FREECAD ASSEMBLY — COMPONENT RECIPES ("YR_ASSEMBLED")

This assembly document has 4 components, labeled P0..P3 below (a component is one placed body or linked part). 4 of them carry a construction recipe — the FreeCAD feature program that regenerates the part from scratch, quoted from this document or its linked companion documents; the rest are supplied as boundary geometry only. No exploded tour is included for this assembly.
COMPONENT P0 — recipe-attached ("Body001", a linked part whose construction recipe lives in a companion FreeCAD document of the same project; that document's serialized recipe follows).
Construction recipe (the companion document, serialized — sketch geometry with constraints, then the solid features built on it; lengths are millimeters unless a unit is written):

FCSTD DOCUMENT  (FreeCAD 1.0R39319 (Git))
Label: knob
License: All rights reserved
LicenseURL: https://en.wikipedia.org/wiki/All_rights_reserved
objects: PartDesign::Chamfer×2, Sketcher::SketchObject×1, PartDesign::Pad×1, PartDesign::Body×1
note: 12 computed .brp shape members not serialized (recipe doc carries the construction recipe); baked Part::Feature solids carry a one-line shape summary decoded from their .brp

FEATURE [Sketcher::SketchObject] Sketch
  ArcFitTolerance = 1e-06
  AttachmentSupport = -> [XY_Plane]
  FullyConstrained = true
  MakeInternals = false
  MapMode = 5
  sketch-geometry (1):
    g0: Circle CenterX=0 CenterY=0 CenterZ=0 NormalX=0 NormalY=0 NormalZ=1 AngleXU=0 Radius=10.5
  constraints (2):
    c: Diameter(g0) = 21
    c: Coincident(g0,g-1)
FEATURE [PartDesign::Pad] Pad
  Direction = (0,0,1)
  Length = 17
  Length2 = 10
  Profile = -> Sketch
  ReferenceAxis = -> Sketch [N_Axis]
  Refine = true
  Suppressed = false
  Type = 0
FEATURE [PartDesign::Chamfer] Chamfer
  Angle = 45
  Base = -> Pad [Edge3]
  BaseFeature = -> Pad
  ChamferType = 0
  FlipDirection = false
  Refine = true
  Size = 1
  Size2 = 1
  SupportTransform = false
  Suppressed = false
  UseAllEdges = false
FEATURE [PartDesign::Chamfer] Chamfer001
  Angle = 45
  Base = -> Chamfer [Edge3]
  BaseFeature = -> Chamfer
  ChamferType = 0
  FlipDirection = false
  Refine = true
  Size = 1
  Size2 = 1
  SupportTransform = false
  Suppressed = false
  UseAllEdges = false
FEATURE [PartDesign::Body] Body
  AllowCompound = false
  Group = -> [Sketch,Pad,Chamfer,Chamfer001]
  Origin = -> Origin
  Tip = -> Chamfer001
COMPONENT P1 — recipe-attached ("ER-OLEDM032-1_new054", a linked part whose construction recipe lives in a companion FreeCAD document of the same project; that document's serialized recipe follows).
Construction recipe (the companion document, serialized — sketch geometry with constraints, then the solid features built on it; lengths are millimeters unless a unit is written):

FCSTD DOCUMENT  (FreeCAD 1.0R39319 (Git))
Label: SSD1322
License: All rights reserved
objects: Part::Feature×54, PartDesign::Body×1, App::Part×1
note: 55 computed .brp shape members not serialized (recipe doc carries the construction recipe); baked Part::Feature solids carry a one-line shape summary decoded from their .brp

FEATURE [PartDesign::Body] Body
  AllowCompound = false
  Origin = -> Origin
FEATURE [Part::Feature] Part__Feature  label="ER-OLEDM032-1_new"
  shape: bbox 100.5 x 33.5 x 1 mm, 110 faces (baked)
FEATURE [Part::Feature] Part__Feature001  label="ER-OLEDM032-1_new001"
  shape: bbox 3.007 x 3.014 x 2.1 mm, 6 faces (baked)
FEATURE [Part::Feature] Part__Feature002  label="ER-OLEDM032-1_new002"
  shape: bbox 3.007 x 3.014 x 2.1 mm, 6 faces (baked)
FEATURE [Part::Feature] Part__Feature003  label="ER-OLEDM032-1_new003"
  shape: bbox 3.007 x 3.014 x 2.1 mm, 6 faces (baked)
FEATURE [Part::Feature] Part__Feature004  label="ER-OLEDM032-1_new004"
  shape: bbox 3.007 x 3.014 x 2.1 mm, 6 faces (baked)
FEATURE [Part::Feature] Part__Feature005  label="ER-OLEDM032-1_new005"
  shape: bbox 3.007 x 3.014 x 2.1 mm, 6 faces (baked)
FEATURE [Part::Feature] Part__Feature006  label="ER-OLEDM032-1_new006"
  shape: bbox 5.7 x 3.24 x 2.3 mm, 6 faces (baked)
FEATURE [Part::Feature] Part__Feature007  label="ER-OLEDM032-1_new007"
  shape: bbox 1.746 x 1.036 x 0.1 mm, 14 faces (baked)
FEATURE [Part::Feature] Part__Feature008  label="ER-OLEDM032-1_new008"
  shape: bbox 1.751 x 1.201 x 0.1 mm, 17 faces (baked)
FEATURE [Part::Feature] Part__Feature009  label="ER-OLEDM032-1_new009"
  shape: bbox 0.1525 x 0.6143 x 0.1 mm, 6 faces (baked)
FEATURE [Part::Feature] Part__Feature010  label="ER-OLEDM032-1_new010"
  shape: bbox 1.792 x 1.506 x 0.1 mm, 12 faces (baked)
FEATURE [Part::Feature] Part__Feature011  label="ER-OLEDM032-1_new011"
  shape: bbox 1.748 x 0.9883 x 0.1 mm, 8 faces (baked)
FEATURE [Part::Feature] Part__Feature012  label="ER-OLEDM032-1_new012"
  shape: bbox 1.746 x 1.036 x 0.1 mm, 14 faces (baked)
FEATURE [Part::Feature] Part__Feature013  label="ER-OLEDM032-1_new013"
  shape: bbox 1.748 x 1.262 x 0.1 mm, 12 faces (baked)
FEATURE [Part::Feature] Part__Feature014  label="ER-OLEDM032-1_new014"
  shape: bbox 1.75 x 1.462 x 0.1 mm, 24 faces (baked)
FEATURE [Part::Feature] Part__Feature015  label="ER-OLEDM032-1_new015"
  shape: bbox 1.795 x 1.062 x 0.1 mm, 12 faces (baked)
FEATURE [Part::Feature] Part__Feature016  label="ER-OLEDM032-1_new016"
  shape: bbox 1.792 x 1.13 x 0.1 mm, 19 faces (baked)
FEATURE [Part::Feature] Part__Feature017  label="ER-OLEDM032-1_new017"
  shape: bbox 1.77 x 1.096 x 0.1 mm, 14 faces (baked)
FEATURE [Part::Feature] Part__Feature018  label="ER-OLEDM032-1_new018"
  shape: bbox 0.1525 x 0.6143 x 0.1 mm, 6 faces (baked)
FEATURE [Part::Feature] Part__Feature019  label="ER-OLEDM032-1_new019"
  shape: bbox 1.748 x 0.9421 x 0.1 mm, 13 faces (baked)
FEATURE [Part::Feature] Part__Feature020  label="ER-OLEDM032-1_new020"
  shape: bbox 57 x 18.36 x 3 mm, 48 faces (baked)
FEATURE [Part::Feature] Part__Feature021  label="ER-OLEDM032-1_new021"
  shape: bbox 85 x 26 x 1.8 mm, 7 faces (baked)
FEATURE [Part::Feature] Part__Feature022  label="ER-OLEDM032-1_new022"
  shape: bbox 89.5 x 30.8 x 3 mm, 60 faces (baked)
FEATURE [Part::Feature] Part__Feature023  label="ER-OLEDM032-1_new023"
  shape: bbox 9.982 x 0.1017 x 0.2 mm, 6 faces (baked)
FEATURE [Part::Feature] Part__Feature024  label="ER-OLEDM032-1_new024"
  shape: bbox 1.086 x 4.946 x 0.2 mm, 5 faces (baked)
FEATURE [Part::Feature] Part__Feature025  label="ER-OLEDM032-1_new025"
  shape: bbox 3.64 x 4.408 x 0.2 mm, 10 faces (baked)
FEATURE [Part::Feature] Part__Feature026  label="ER-OLEDM032-1_new026"
  shape: bbox 2.025 x 2.903 x 0.2 mm, 8 faces (baked)
FEATURE [Part::Feature] Part__Feature027  label="ER-OLEDM032-1_new027"
  shape: bbox 0.9724 x 1.521 x 0.2 mm, 20 faces (baked)
FEATURE [Part::Feature] Part__Feature028  label="ER-OLEDM032-1_new028"
  shape: bbox 0.9011 x 1.106 x 0.2 mm, 15 faces (baked)
FEATURE [Part::Feature] Part__Feature029  label="ER-OLEDM032-1_new029"
  shape: bbox 0.1976 x 1.085 x 0.2 mm, 6 faces (baked)
FEATURE [Part::Feature] Part__Feature030  label="ER-OLEDM032-1_new030"
  shape: bbox 0.1915 x 0.1915 x 0.2 mm, 6 faces (baked)
FEATURE [Part::Feature] Part__Feature031  label="ER-OLEDM032-1_new031"
  shape: bbox 0.9318 x 1.122 x 0.2 mm, 20 faces (baked)
FEATURE [Part::Feature] Part__Feature032  label="ER-OLEDM032-1_new032"
  shape: bbox 0.1976 x 1.085 x 0.2 mm, 6 faces (baked)
FEATURE [Part::Feature] Part__Feature033  label="ER-OLEDM032-1_new033"
  shape: bbox 0.1915 x 0.1915 x 0.2 mm, 6 faces (baked)
FEATURE [Part::Feature] Part__Feature034  label="ER-OLEDM032-1_new034"
  shape: bbox 1.344 x 1.488 x 0.2 mm, 21 faces (baked)
FEATURE [Part::Feature] Part__Feature035  label="ER-OLEDM032-1_new035"
  shape: bbox 0.5399 x 1.474 x 0.2 mm, 18 faces (baked)
FEATURE [Part::Feature] Part__Feature036  label="ER-OLEDM032-1_new036"
  shape: bbox 0.9318 x 1.122 x 0.2 mm, 20 faces (baked)
FEATURE [Part::Feature] Part__Feature037  label="ER-OLEDM032-1_new037"
  shape: bbox 1.01 x 1.123 x 0.2 mm, 25 faces (baked)
FEATURE [Part::Feature] Part__Feature038  label="ER-OLEDM032-1_new038"
  shape: bbox 1.151 x 1.491 x 0.2 mm, 14 faces (baked)
FEATURE [Part::Feature] Part__Feature039  label="ER-OLEDM032-1_new039"
  shape: bbox 0.8271 x 0.5902 x 0.2 mm, 27 faces (baked)
FEATURE [Part::Feature] Part__Feature040  label="ER-OLEDM032-1_new040"
  shape: bbox 0.5683 x 0.5958 x 0.2 mm, 18 faces (baked)
FEATURE [Part::Feature] Part__Feature041  label="ER-OLEDM032-1_new041"
  shape: bbox 0.5538 x 0.5958 x 0.2 mm, 20 faces (baked)
FEATURE [Part::Feature] Part__Feature042  label="ER-OLEDM032-1_new042"
  shape: bbox 0.1556 x 0.1438 x 0.2 mm, 6 faces (baked)
FEATURE [Part::Feature] Part__Feature043  label="ER-OLEDM032-1_new043"
  shape: bbox 0.6077 x 0.7614 x 0.2 mm, 15 faces (baked)
FEATURE [Part::Feature] Part__Feature044  label="ER-OLEDM032-1_new044"
  shape: bbox 0.5496 x 0.5962 x 0.2 mm, 31 faces (baked)
FEATURE [Part::Feature] Part__Feature045  label="ER-OLEDM032-1_new045"
  shape: bbox 0.1487 x 0.8679 x 0.2 mm, 6 faces (baked)
FEATURE [Part::Feature] Part__Feature046  label="ER-OLEDM032-1_new046"
  shape: bbox 0.544 x 0.7703 x 0.2 mm, 22 faces (baked)
FEATURE [Part::Feature] Part__Feature047  label="ER-OLEDM032-1_new047"
  shape: bbox 0.4994 x 0.5958 x 0.2 mm, 30 faces (baked)
FEATURE [Part::Feature] Part__Feature048  label="ER-OLEDM032-1_new048"
  shape: bbox 0.1467 x 0.577 x 0.2 mm, 6 faces (baked)
FEATURE [Part::Feature] Part__Feature049  label="ER-OLEDM032-1_new049"
  shape: bbox 0.1438 x 0.153 x 0.2 mm, 6 faces (baked)
FEATURE [Part::Feature] Part__Feature050  label="ER-OLEDM032-1_new050"
  shape: bbox 0.5356 x 0.8786 x 0.2 mm, 21 faces (baked)
FEATURE [Part::Feature] Part__Feature051  label="ER-OLEDM032-1_new051"
  shape: bbox 0.6077 x 0.7614 x 0.2 mm, 15 faces (baked)
FEATURE [Part::Feature] Part__Feature052  label="ER-OLEDM032-1_new052"
  shape: bbox 0.5313 x 0.5881 x 0.2 mm, 17 faces (baked)
FEATURE [Part::Feature] Part__Feature053  label="ER-OLEDM032-1_new053"
  shape: bbox 0.546 x 0.8759 x 0.2 mm, 22 faces (baked)
FEATURE [App::Part] ER_OLEDM032_1_new  label="ER-OLEDM032-1_new054"
  Group = -> [Part__Feature,Part__Feature001,Part__Feature002,Part__Feature003,Part__Feature004,Part__Feature005,Part__Feature006,Part__Feature007,Part__Feature008,Part__Feature009,Part__Feature010,Part__Feature011,Part__Feature012,Part__Feature013,Part__Feature014,Part__Feature015,Part__Feature016,Part__Feature017,Part__Feature018,Part__Feature019,Part__Feature020,Part__Feature021,Part__Feature022,+31 more]
  Origin = -> Origin001
COMPONENT P2 — recipe-attached ("PinHeader_2x08_P254mm_Vertical", a linked part whose construction recipe lives in a companion FreeCAD document of the same project; that document's serialized recipe follows).
Construction recipe (the companion document, serialized — sketch geometry with constraints, then the solid features built on it; lengths are millimeters unless a unit is written):

FCSTD DOCUMENT  (FreeCAD 1.0R39319 (Git))
Label: pin_header_2x08
License: All rights reserved
objects: PartDesign::Body×1, Part::Feature×1
note: 2 computed .brp shape members not serialized (recipe doc carries the construction recipe); baked Part::Feature solids carry a one-line shape summary decoded from their .brp

FEATURE [PartDesign::Body] Body
  AllowCompound = false
  Origin = -> Origin
FEATURE [Part::Feature] Part__Feature  label="PinHeader_2x08_P254mm_Vertical"
  shape: bbox 5.08 x 20.32 x 11.54 mm, 340 faces (baked)
COMPONENT P3 — recipe-attached ("YR", a linked part whose construction recipe lives in a companion FreeCAD document of the same project; that document's serialized recipe follows).
Construction recipe (the companion document, serialized — sketch geometry with constraints, then the solid features built on it; lengths are millimeters unless a unit is written):

FCSTD DOCUMENT  (FreeCAD 1.0R39319 (Git))
Label: YR1
License: All rights reserved
objects: Part::Feature×75, App::Link×22, App::Part×7, PartDesign::CoordinateSystem×1, Sketcher::SketchObject×1
note: 78 computed .brp shape members not serialized (recipe doc carries the construction recipe); baked Part::Feature solids carry a one-line shape summary decoded from their .brp

FEATURE [PartDesign::CoordinateSystem] Local_CS_ce90
  AttacherType = Attacher::AttachEngine3D
  MapMode = 2
FEATURE [Part::Feature] Pcb_ce90
  shape: bbox 131.8 x 33.06 x 1.6 mm, 115 faces (baked)
FEATURE [Sketcher::SketchObject] PCB_Sketch_ce90
  ArcFitTolerance = 1e-06
  FullyConstrained = false
  MakeInternals = false
  sketch-geometry (4):
    g0: LineSegment StartX=75.75 StartY=-49.971 StartZ=0 EndX=207.5 EndY=-49.971 EndZ=0
    g1: LineSegment StartX=207.5 StartY=-49.971 StartZ=0 EndX=207.5 EndY=-83.029 EndZ=0
    g2: LineSegment StartX=207.5 StartY=-83.029 StartZ=0 EndX=75.75 EndY=-83.029 EndZ=0
    g3: LineSegment StartX=75.75 StartY=-83.029 StartZ=0 EndX=75.75 EndY=-49.971 EndZ=0
  constraints (4):
    c: Coincident(g2,g3)
    c: Coincident(g0,g3)
    c: Coincident(g1,g2)
    c: Coincident(g0,g1)
FEATURE [App::Part] Board_Geoms_ce90
  Group = -> [Pcb_ce90,PCB_Sketch_ce90]
  Origin = -> Origin
FEATURE [Part::Feature] Shape  label="R8_R_1206_3216Metric_849fe551dc66"
  Placement = pos=(86.106,-79.02,0) rot=(0,0,1;1.5708rad)
  shape: bbox 1.6 x 3.2 x 0.55 mm, 26 faces (baked)
FEATURE [Part::Feature] Shape001  label="C6_C_1206_3216Metric_5806ac7bf1ee"
  Placement = pos=(93.5,-59.3125,0) rot=(0,0,1;1.5708rad)
  shape: bbox 1.6 x 3.2 x 1.6 mm, 28 faces (baked)
FEATURE [Part::Feature] Shape002  label="U3_SOT-223_b71a6138f545"
  Placement = pos=(186.75,-55.65,0) rot=(0,0,1;1.5708rad)
  shape: bbox 6.5 x 7 x 1.7 mm, 75 faces (baked)
FEATURE [App::Link] C6_C_1206_3216Metric_5806ac7bf1ee_ln_  label="C4_C_1206_3216Metric_0b2260ff10fb"
  LinkPlacement = pos=(98.5,-59.25,0) rot=(0,0,1;1.5708rad)
  LinkedObject = -> Shape001
  Placement = pos=(98.5,-59.25,0) rot=(0,0,1;1.5708rad)
FEATURE [Part::Feature] Part__Feature  label="ESP32-S3-WROOM-1"
  shape: bbox 15 x 5.5 x 0.2 mm, 30 faces (baked)
FEATURE [Part::Feature] Part__Feature001  label="ESP32-S3-WROOM-002"
  shape: bbox 18 x 25.5 x 0.8 mm, 451 faces (baked)
FEATURE [Part::Feature] Part__Feature002  label="ESP32-S3-WROOM-003"
  shape: bbox 15.8 x 17.6 x 2.3 mm, 20 faces (baked)
FEATURE [Part::Feature] Part__Feature003  label="ESP32-S3-WROOM-004"
  shape: bbox 0.85 x 0.9 x 0.8 mm, 18 faces (baked)
FEATURE [Part::Feature] Part__Feature004  label="ESP32-S3-WROOM-005"
  shape: bbox 0.85 x 0.9 x 0.8 mm, 18 faces (baked)
FEATURE [Part::Feature] Part__Feature005  label="ESP32-S3-WROOM-006"
  shape: bbox 0.85 x 0.9 x 0.8 mm, 18 faces (baked)
FEATURE [Part::Feature] Part__Feature006  label="ESP32-S3-WROOM-007"
  shape: bbox 0.85 x 0.9 x 0.8 mm, 18 faces (baked)
FEATURE [Part::Feature] Part__Feature007  label="ESP32-S3-WROOM-008"
  shape: bbox 0.85 x 0.9 x 0.8 mm, 18 faces (baked)
FEATURE [Part::Feature] Part__Feature008  label="ESP32-S3-WROOM-009"
  shape: bbox 0.85 x 0.9 x 0.8 mm, 18 faces (baked)
FEATURE [Part::Feature] Part__Feature009  label="ESP32-S3-WROOM-010"
  shape: bbox 0.85 x 0.9 x 0.8 mm, 18 faces (baked)
FEATURE [Part::Feature] Part__Feature010  label="ESP32-S3-WROOM-011"
  shape: bbox 0.85 x 0.9 x 0.8 mm, 18 faces (baked)
FEATURE [Part::Feature] Part__Feature011  label="ESP32-S3-WROOM-012"
  shape: bbox 0.85 x 0.9 x 0.8 mm, 18 faces (baked)
FEATURE [Part::Feature] Part__Feature012  label="ESP32-S3-WROOM-013"
  shape: bbox 0.85 x 0.9 x 0.8 mm, 18 faces (baked)
FEATURE [Part::Feature] Part__Feature013  label="ESP32-S3-WROOM-014"
  shape: bbox 0.85 x 0.9 x 0.8 mm, 18 faces (baked)
FEATURE [Part::Feature] Part__Feature014  label="ESP32-S3-WROOM-015"
  shape: bbox 0.85 x 0.9 x 0.8 mm, 18 faces (baked)
FEATURE [Part::Feature] Part__Feature015  label="ESP32-S3-WROOM-016"
  shape: bbox 0.85 x 0.9 x 0.8 mm, 18 faces (baked)
FEATURE [Part::Feature] Part__Feature016  label="ESP32-S3-WROOM-017"
  shape: bbox 0.9 x 0.85 x 0.8 mm, 18 faces (baked)
FEATURE [Part::Feature] Part__Feature017  label="ESP32-S3-WROOM-018"
  shape: bbox 0.9 x 0.85 x 0.8 mm, 18 faces (baked)
FEATURE [Part::Feature] Part__Feature018  label="ESP32-S3-WROOM-019"
  shape: bbox 0.9 x 0.85 x 0.8 mm, 18 faces (baked)
FEATURE [Part::Feature] Part__Feature019  label="ESP32-S3-WROOM-020"
  shape: bbox 0.9 x 0.85 x 0.8 mm, 18 faces (baked)
FEATURE [Part::Feature] Part__Feature020  label="ESP32-S3-WROOM-021"
  shape: bbox 0.9 x 0.85 x 0.8 mm, 18 faces (baked)
FEATURE [Part::Feature] Part__Feature021  label="ESP32-S3-WROOM-022"
  shape: bbox 0.9 x 0.85 x 0.8 mm, 18 faces (baked)
FEATURE [Part::Feature] Part__Feature022  label="ESP32-S3-WROOM-023"
  shape: bbox 0.85 x 0.9 x 0.8 mm, 18 faces (baked)
FEATURE [Part::Feature] Part__Feature023  label="ESP32-S3-WROOM-024"
  shape: bbox 0.85 x 0.9 x 0.8 mm, 18 faces (baked)
FEATURE [Part::Feature] Part__Feature024  label="ESP32-S3-WROOM-025"
  shape: bbox 0.85 x 0.9 x 0.8 mm, 18 faces (baked)
FEATURE [Part::Feature] Part__Feature025  label="ESP32-S3-WROOM-026"
  shape: bbox 0.85 x 0.9 x 0.8 mm, 18 faces (baked)
FEATURE [Part::Feature] Part__Feature026  label="ESP32-S3-WROOM-027"
  shape: bbox 0.85 x 0.9 x 0.8 mm, 18 faces (baked)
FEATURE [Part::Feature] Part__Feature027  label="ESP32-S3-WROOM-028"
  shape: bbox 0.85 x 0.9 x 0.8 mm, 18 faces (baked)
FEATURE [Part::Feature] Part__Feature028  label="ESP32-S3-WROOM-029"
  shape: bbox 0.85 x 0.9 x 0.8 mm, 18 faces (baked)
FEATURE [Part::Feature] Part__Feature029  label="ESP32-S3-WROOM-030"
  shape: bbox 0.85 x 0.9 x 0.8 mm, 18 faces (baked)
FEATURE [Part::Feature] Part__Feature030  label="ESP32-S3-WROOM-031"
  shape: bbox 0.85 x 0.9 x 0.8 mm, 18 faces (baked)
FEATURE [Part::Feature] Part__Feature031  label="ESP32-S3-WROOM-032"
  shape: bbox 0.85 x 0.9 x 0.8 mm, 18 faces (baked)
FEATURE [Part::Feature] Part__Feature032  label="ESP32-S3-WROOM-033"
  shape: bbox 0.85 x 0.9 x 0.8 mm, 18 faces (baked)
FEATURE [Part::Feature] Part__Feature033  label="ESP32-S3-WROOM-034"
  shape: bbox 0.85 x 0.9 x 0.8 mm, 18 faces (baked)
FEATURE [Part::Feature] Part__Feature034  label="ESP32-S3-WROOM-035"
  shape: bbox 0.85 x 0.9 x 0.8 mm, 18 faces (baked)
FEATURE [Part::Feature] Part__Feature035  label="ESP32-S3-WROOM-036"
  shape: bbox 0.85 x 0.9 x 0.8 mm, 18 faces (baked)
FEATURE [Part::Feature] Part__Feature036  label="ESP32-S3-WROOM-037"
  shape: bbox 0.9 x 0.85 x 0.8 mm, 18 faces (baked)
FEATURE [Part::Feature] Part__Feature037  label="ESP32-S3-WROOM-038"
  shape: bbox 0.9 x 0.85 x 0.8 mm, 18 faces (baked)
FEATURE [Part::Feature] Part__Feature038  label="ESP32-S3-WROOM-039"
  shape: bbox 0.9 x 0.85 x 0.8 mm, 18 faces (baked)
FEATURE [Part::Feature] Part__Feature039  label="ESP32-S3-WROOM-040"
  shape: bbox 0.9 x 0.85 x 0.8 mm, 18 faces (baked)
FEATURE [Part::Feature] Part__Feature040  label="ESP32-S3-WROOM-041"
  shape: bbox 0.9 x 0.85 x 0.8 mm, 18 faces (baked)
FEATURE [Part::Feature] Part__Feature041  label="ESP32-S3-WROOM-042"
  shape: bbox 0.9 x 0.85 x 0.8 mm, 18 faces (baked)
FEATURE [Part::Feature] Part__Feature042  label="ESP32-S3-WROOM-043"
  shape: bbox 0.85 x 0.9 x 0.8 mm, 18 faces (baked)
FEATURE [Part::Feature] Part__Feature043  label="ESP32-S3-WROOM-044"
  shape: bbox 0.9 x 0.9 x 0.4 mm, 6 faces (baked)
FEATURE [Part::Feature] Part__Feature044  label="ESP32-S3-WROOM-045"
  shape: bbox 0.9 x 0.9 x 0.4 mm, 6 faces (baked)
FEATURE [Part::Feature] Part__Feature045  label="ESP32-S3-WROOM-046"
  shape: bbox 0.9 x 0.9 x 0.4 mm, 6 faces (baked)
FEATURE [Part::Feature] Part__Feature046  label="ESP32-S3-WROOM-047"
  shape: bbox 0.9 x 0.9 x 0.4 mm, 6 faces (baked)
FEATURE [Part::Feature] Part__Feature047  label="ESP32-S3-WROOM-048"
  shape: bbox 0.9 x 0.9 x 0.4 mm, 6 faces (baked)
FEATURE [Part::Feature] Part__Feature048  label="ESP32-S3-WROOM-049"
  shape: bbox 0.9 x 0.9 x 0.4 mm, 6 faces (baked)
FEATURE [Part::Feature] Part__Feature049  label="ESP32-S3-WROOM-050"
  shape: bbox 0.9 x 0.9 x 0.4 mm, 6 faces (baked)
FEATURE [Part::Feature] Part__Feature050  label="ESP32-S3-WROOM-051"
  shape: bbox 0.9 x 0.9 x 0.4 mm, 6 faces (baked)
FEATURE [Part::Feature] Part__Feature051  label="ESP32-S3-WROOM-052"
  shape: bbox 0.9 x 0.9 x 0.4 mm, 6 faces (baked)
FEATURE [App::Part] ESP32_S3_WROOM_1  label="U2_ESP32-S3-WROOM-053_bd523d393ef9"
  Group = -> [Part__Feature,Part__Feature001,Part__Feature002,Part__Feature003,Part__Feature004,Part__Feature005,Part__Feature006,Part__Feature007,Part__Feature008,Part__Feature009,Part__Feature010,Part__Feature011,Part__Feature012,Part__Feature013,Part__Feature014,Part__Feature015,Part__Feature016,Part__Feature017,Part__Feature018,Part__Feature019,Part__Feature020,Part__Feature021,Part__Feature022,+29 more]
  Origin = -> Origin008
  Placement = pos=(150,-63.14,0) rot=(0,0,1;0rad)
FEATURE [App::Link] C6_C_1206_3216Metric_5806ac7bf1ee_ln_001  label="C8_C_1206_3216Metric_3bbef69fec14"
  LinkPlacement = pos=(98.5,-74.5625,0) rot=(0,0,-1;1.5708rad)
  LinkedObject = -> Shape001
  Placement = pos=(98.5,-74.5625,0) rot=(0,0,-1;1.5708rad)
FEATURE [Part::Feature] Shape003  label="J5_PinHeader_1x05_P254mm_Vertical_ae4142e8ed21"
  Placement = pos=(195.072,-59.944,0) rot=(0,0,1;1.5708rad)
  shape: bbox 12.7 x 2.54 x 11.54 mm, 124 faces (baked)
FEATURE [App::Link] U3_SOT_223_b71a6138f545_ln_  label="U1_SOT-223_6c20c0ed07f9"
  LinkPlacement = pos=(112.2,-59.715,0) rot=(0,0,1;1.5708rad)
  LinkedObject = -> Shape002
  Placement = pos=(112.2,-59.715,0) rot=(0,0,1;1.5708rad)
FEATURE [App::Link] J5_PinHeader_1x05_P254mm_Vertical_ae4142e8ed21_ln_  label="J4_PinHeader_1x05_P254mm_Vertical_96848d7125c2"
  LinkPlacement = pos=(195.072,-65.278,0) rot=(0,0,1;1.5708rad)
  LinkedObject = -> Shape003
  Placement = pos=(195.072,-65.278,0) rot=(0,0,1;1.5708rad)
FEATURE [Part::Feature] Shape004  label="J6_PinHeader_1x14_P254mm_Vertical_bfc407b08b14"
  Placement = pos=(107.95,-81.28,0) rot=(0,0,1;1.5708rad)
  shape: bbox 35.56 x 2.54 x 11.54 mm, 340 faces (baked)
FEATURE [App::Link] R8_R_1206_3216Metric_849fe551dc66_ln_  label="R4_R_1206_3216Metric_ffd76c8efa39"
  LinkPlacement = pos=(98.5,-66.8,0) rot=(0,0,1;1.5708rad)
  LinkedObject = -> Shape
  Placement = pos=(98.5,-66.8,0) rot=(0,0,1;1.5708rad)
FEATURE [App::Link] J5_PinHeader_1x05_P254mm_Vertical_ae4142e8ed21_ln_001  label="J7_PinHeader_1x05_P254mm_Vertical_28aa004d9f87"
  LinkPlacement = pos=(108.84,-73.66,0) rot=(0,0,1;1.5708rad)
  LinkedObject = -> Shape003
  Placement = pos=(108.84,-73.66,0) rot=(0,0,1;1.5708rad)
FEATURE [Part::Feature] Shape005  label="S2_SW_SPST_TS-1088-xR025_609cbf66d0a0"
  Placement = pos=(179.525,-53.25,0) rot=(0,0,1;0rad)
  shape: bbox 5 x 3 x 2.5 mm, 94 faces (baked)
FEATURE [App::Link] C6_C_1206_3216Metric_5806ac7bf1ee_ln_002  label="C10_C_1206_3216Metric_dee7ef7d7bcf"
  LinkPlacement = pos=(193,-54.3125,0) rot=(0,0,-1;1.5708rad)
  LinkedObject = -> Shape001
  Placement = pos=(193,-54.3125,0) rot=(0,0,-1;1.5708rad)
FEATURE [Part::Feature] Shape006  label="J8_PinHeader_1x06_P254mm_Vertical_6df93f4f9b2e"
  Placement = pos=(166.878,-72.898,0) rot=(0,0,1;1.5708rad)
  shape: bbox 15.24 x 2.54 x 11.54 mm, 148 faces (baked)
FEATURE [App::Link] R8_R_1206_3216Metric_849fe551dc66_ln_001  label="R9_R_1206_3216Metric_fa8baf5cef4c"
  LinkPlacement = pos=(179.552,-63.246,0) rot=(0,0,1;3.14159rad)
  LinkedObject = -> Shape
  Placement = pos=(179.552,-63.246,0) rot=(0,0,1;3.14159rad)
FEATURE [App::Link] R8_R_1206_3216Metric_849fe551dc66_ln_002  label="R5_R_1206_3216Metric_fcb516a619e7"
  LinkPlacement = pos=(87.402,-54.102,0) rot=(0,0,1;3.14159rad)
  LinkedObject = -> Shape
  Placement = pos=(87.402,-54.102,0) rot=(0,0,1;3.14159rad)
FEATURE [Part::Feature] Shape007  label="C2_CP_Elec_4x39_5d7db91c04dc"
  Placement = pos=(121.18,-62.23,0) rot=(0,0,1;0rad)
  shape: bbox 5.738 x 5.462 x 3.9 mm, 41 faces (baked)
FEATURE [App::Link] C2_CP_Elec_4x39_5d7db91c04dc_ln_  label="C12_CP_Elec_4x39_d26d4e954a9b"
  LinkPlacement = pos=(185.7,-63.25,0) rot=(0,0,1;3.14159rad)
  LinkedObject = -> Shape007
  Placement = pos=(185.7,-63.25,0) rot=(0,0,1;3.14159rad)
FEATURE [App::Link] C6_C_1206_3216Metric_5806ac7bf1ee_ln_003  label="C11_C_1206_3216Metric_4dca7c0ed160"
  LinkPlacement = pos=(190.75,-64.5545,0) rot=(0,0,-1;1.5708rad)
  LinkedObject = -> Shape001
  Placement = pos=(190.75,-64.5545,0) rot=(0,0,-1;1.5708rad)
FEATURE [App::Link] C6_C_1206_3216Metric_5806ac7bf1ee_ln_004  label="C3_C_1206_3216Metric_46be7cb0c2e6"
  LinkPlacement = pos=(167.188,-59,0) rot=(0,0,1;0rad)
  LinkedObject = -> Shape001
  Placement = pos=(167.188,-59,0) rot=(0,0,1;0rad)
FEATURE [App::Link] R8_R_1206_3216Metric_849fe551dc66_ln_003  label="R2_R_1206_3216Metric_9dcc8021d4c6"
  LinkPlacement = pos=(93.5,-66.8,0) rot=(0,0,1;1.5708rad)
  LinkedObject = -> Shape
  Placement = pos=(93.5,-66.8,0) rot=(0,0,1;1.5708rad)
FEATURE [App::Link] R8_R_1206_3216Metric_849fe551dc66_ln_004  label="R7_R_1206_3216Metric_718dacf507a8"
  LinkPlacement = pos=(83.566,-79.02,0) rot=(0,0,1;1.5708rad)
  LinkedObject = -> Shape
  Placement = pos=(83.566,-79.02,0) rot=(0,0,1;1.5708rad)
FEATURE [App::Link] R8_R_1206_3216Metric_849fe551dc66_ln_005  label="R1_R_1206_3216Metric_af3528704da6"
  LinkPlacement = pos=(172.45,-58.928,0) rot=(0,0,1;0rad)
  LinkedObject = -> Shape
  Placement = pos=(172.45,-58.928,0) rot=(0,0,1;0rad)
FEATURE [App::Link] C6_C_1206_3216Metric_5806ac7bf1ee_ln_005  label="C5_C_1206_3216Metric_796cf0bfd849"
  LinkPlacement = pos=(96,-59.3125,0) rot=(0,0,1;1.5708rad)
  LinkedObject = -> Shape001
  Placement = pos=(96,-59.3125,0) rot=(0,0,1;1.5708rad)
FEATURE [App::Link] C6_C_1206_3216Metric_5806ac7bf1ee_ln_006  label="C1_C_1206_3216Metric_4dcc9a78151c"
  LinkPlacement = pos=(121.938,-56.25,0) rot=(0,0,1;0rad)
  LinkedObject = -> Shape001
  Placement = pos=(121.938,-56.25,0) rot=(0,0,1;0rad)
FEATURE [App::Link] C6_C_1206_3216Metric_5806ac7bf1ee_ln_007  label="C7_C_1206_3216Metric_ccd00724a912"
  LinkPlacement = pos=(167.188,-63.75,0) rot=(0,0,1;0rad)
  LinkedObject = -> Shape001
  Placement = pos=(167.188,-63.75,0) rot=(0,0,1;0rad)
FEATURE [App::Link] R8_R_1206_3216Metric_849fe551dc66_ln_006  label="R3_R_1206_3216Metric_c2cdd239b57d"
  LinkPlacement = pos=(96,-66.8,0) rot=(0,0,1;1.5708rad)
  LinkedObject = -> Shape
  Placement = pos=(96,-66.8,0) rot=(0,0,1;1.5708rad)
FEATURE [App::Link] R8_R_1206_3216Metric_849fe551dc66_ln_007  label="R6_R_1206_3216Metric_6c74b1d05212"
  LinkPlacement = pos=(172.45,-63.75,0) rot=(0,0,1;0rad)
  LinkedObject = -> Shape
  Placement = pos=(172.45,-63.75,0) rot=(0,0,1;0rad)
FEATURE [Part::Feature] Shape008  label="J1_PinHeader_1x03_P254mm_Vertical_84979ea4283d"
  Placement = pos=(162.56,-64.135,0) rot=(0,0,1;3.14159rad)
  shape: bbox 2.54 x 7.62 x 11.54 mm, 76 faces (baked)
FEATURE [Part::Feature] Shape009  label="J2_JST_B2B_XH_A_83992c19cd27"
  Placement = pos=(129.58,-60,0) rot=(0,0,1;0rad)
  shape: bbox 7.4 x 5.75 x 10.4 mm, 89 faces (baked)
FEATURE [App::Link] S2_SW_SPST_TS_1088_xR025_609cbf66d0a0_ln_  label="S1_SW_SPST_TS-1088-xR025_2a6c9a76728f"
  LinkPlacement = pos=(179.5,-57.5,0) rot=(0,0,1;0rad)
  LinkedObject = -> Shape005
  Placement = pos=(179.5,-57.5,0) rot=(0,0,1;0rad)
FEATURE [Part::Feature] Shape010  label="J9_PinHeader_1x07_P254mm_Vertical_f38221eea414"
  Placement = pos=(166.878,-69.342,0) rot=(0,0,1;1.5708rad)
  shape: bbox 17.78 x 2.54 x 11.54 mm, 172 faces (baked)
FEATURE [App::Link] C2_CP_Elec_4x39_5d7db91c04dc_ln_001  label="C9_CP_Elec_4x39_77bc80d501f3"
  LinkPlacement = pos=(93.95,-74.5,0) rot=(0,0,1;3.14159rad)
  LinkedObject = -> Shape007
  Placement = pos=(93.95,-74.5,0) rot=(0,0,1;3.14159rad)
FEATURE [App::Part] Top_ce90
  Group = -> [Shape,Shape001,Shape002,C6_C_1206_3216Metric_5806ac7bf1ee_ln_,ESP32_S3_WROOM_1,C6_C_1206_3216Metric_5806ac7bf1ee_ln_001,Shape003,U3_SOT_223_b71a6138f545_ln_,J5_PinHeader_1x05_P254mm_Vertical_ae4142e8ed21_ln_,Shape004,R8_R_1206_3216Metric_849fe551dc66_ln_,J5_PinHeader_1x05_P254mm_Vertical_ae4142e8ed21_ln_001,Shape005,C6_C_1206_3216Metric_5806ac7bf1ee_ln_002,Shape006,+19 more]
  Origin = -> Origin003
FEATURE [Part::Feature] Shape011  label="J3_PinSocket_2x08_P2.54mm_Vertical_4a1cc58c5cdd"
  Placement = pos=(104.29,-74.89,-1.6) rot=(1,0,0;3.14159rad)
  shape: bbox 5.08 x 20.32 x 11.6 mm, 426 faces (baked)
FEATURE [Part::Feature] Part__Feature052  label="EC11_Rotary_Encoder_Switched"
  shape: bbox 1.5 x 1.93 x 7.07 mm, 34 faces (baked)
FEATURE [Part::Feature] Part__Feature053  label="EC11_Rotary_Encoder_Switched001"
  shape: bbox 1.5 x 1.93 x 7.07 mm, 34 faces (baked)
FEATURE [Part::Feature] Part__Feature054  label="EC11_Rotary_Encoder_Switched002"
  shape: bbox 1.5 x 1.93 x 7.07 mm, 34 faces (baked)
FEATURE [Part::Feature] Part__Feature055  label="EC11_Rotary_Encoder_Switched003"
  shape: bbox 1.5 x 1.93 x 7.07 mm, 34 faces (baked)
FEATURE [Part::Feature] Part__Feature056  label="EC11_Rotary_Encoder_Switched004"
  shape: bbox 1.5 x 1.93 x 7.07 mm, 34 faces (baked)
FEATURE [Part::Feature] Part__Feature057  label="EC11_Rotary_Encoder_Switched005"
  shape: bbox 13.1 x 12 x 9.87 mm, 116 faces (baked)
FEATURE [Part::Feature] Part__Feature058  label="EC11_Rotary_Encoder_Switched006"
  shape: bbox 11.8 x 12 x 1.6 mm, 18 faces (baked)
FEATURE [Part::Feature] Part__Feature059  label="EC11_Rotary_Encoder_Switched007"
  shape: bbox 11.8 x 12 x 3.4 mm, 82 faces (baked)
FEATURE [Part::Feature] Part__Feature060  label="EC11_Rotary_Encoder_Switched008"
  shape: bbox 11.8 x 12.5 x 8.743 mm, 73 faces (baked)
FEATURE [Part::Feature] Part__Feature061  label="EC11_Rotary_Encoder_Switched009"
  shape: bbox 5.658 x 5.782 x 13.3 mm, 102 faces (baked)
FEATURE [App::Part] EC11_Rotary_Encoder_Switched  label="SW1_EC11_Rotary_Encoder_Switched010_689899471fdf[2]"
  Group = -> [Part__Feature052,Part__Feature053,Part__Feature054,Part__Feature055,Part__Feature056,Part__Feature057,Part__Feature058,Part__Feature059,Part__Feature060,Part__Feature061]
  Origin = -> Origin009
  Placement = pos=(83.5,-66.5,-1.6) rot=(0,1,0;3.14159rad)
FEATURE [App::Part] Bot_ce90
  Group = -> [Shape011,EC11_Rotary_Encoder_Switched]
  Origin = -> Origin004
FEATURE [App::Part] Step_Models_ce90
  Group = -> [Top_ce90,Bot_ce90]
  Origin = -> Origin002
FEATURE [App::Part] Board_ce90  label="YR"
  Group = -> [Local_CS_ce90,Board_Geoms_ce90,Step_Models_ce90]
  Origin = -> Origin001
PROVENANCE & LICENSES
A FreeCAD (.FCStd) document from a public repository crawl; recipes are the document's own serialized feature recipes (and, for linked parts, companion documents' recipes).
License: mit.
